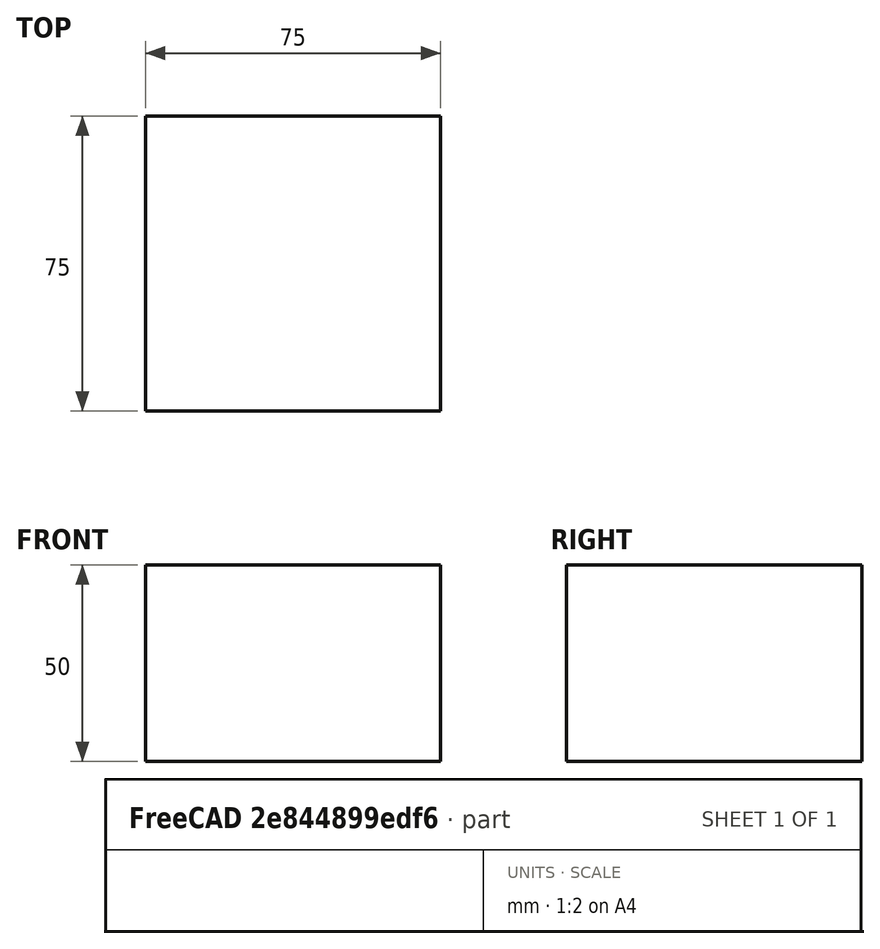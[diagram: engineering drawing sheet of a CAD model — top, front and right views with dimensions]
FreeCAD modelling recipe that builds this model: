
FCSTD DOCUMENT  (FreeCAD 0.15R4671 (Git))
Label: Square Bar 75 EN10059 S235JR
License: All rights reserved
LicenseURL: http://en.wikipedia.org/wiki/All_rights_reserved
objects: Sketcher::SketchObject×1, Part::Extrusion×1
note: 2 computed .brp shape members not serialized (recipe doc carries the construction recipe); baked Part::Feature solids carry a one-line shape summary decoded from their .brp

FEATURE [Sketcher::SketchObject] Sketch
  sketch-geometry (4):
    g0: LineSegment StartX=-37.5 StartY=-37.5 StartZ=0 EndX=37.5 EndY=-37.5 EndZ=0
    g1: LineSegment StartX=37.5 StartY=-37.5 StartZ=0 EndX=37.5 EndY=37.5 EndZ=0
    g2: LineSegment StartX=37.5 StartY=37.5 StartZ=0 EndX=-37.5 EndY=37.5 EndZ=0
    g3: LineSegment StartX=-37.5 StartY=37.5 StartZ=0 EndX=-37.5 EndY=-37.5 EndZ=0
  constraints (12):
    c: Coincident(g0,g1)
    c: Coincident(g1,g2)
    c: Coincident(g2,g3)
    c: Coincident(g3,g0)
    c: Horizontal(g0)
    c: Horizontal(g2)
    c: Vertical(g1)
    c: Vertical(g3)
    c: Symmetric(g1,g0,g-1)
    c: Symmetric(g2,g1,g-2)
    c: Equal(g1,g2)
    c: DistanceY(g1) = 75
FEATURE [Part::Extrusion] Extrude  label="Square Bar 75 EN10059 S235JR"
  Base = -> Sketch
  Dir = (0,0,50)
  Solid = true
